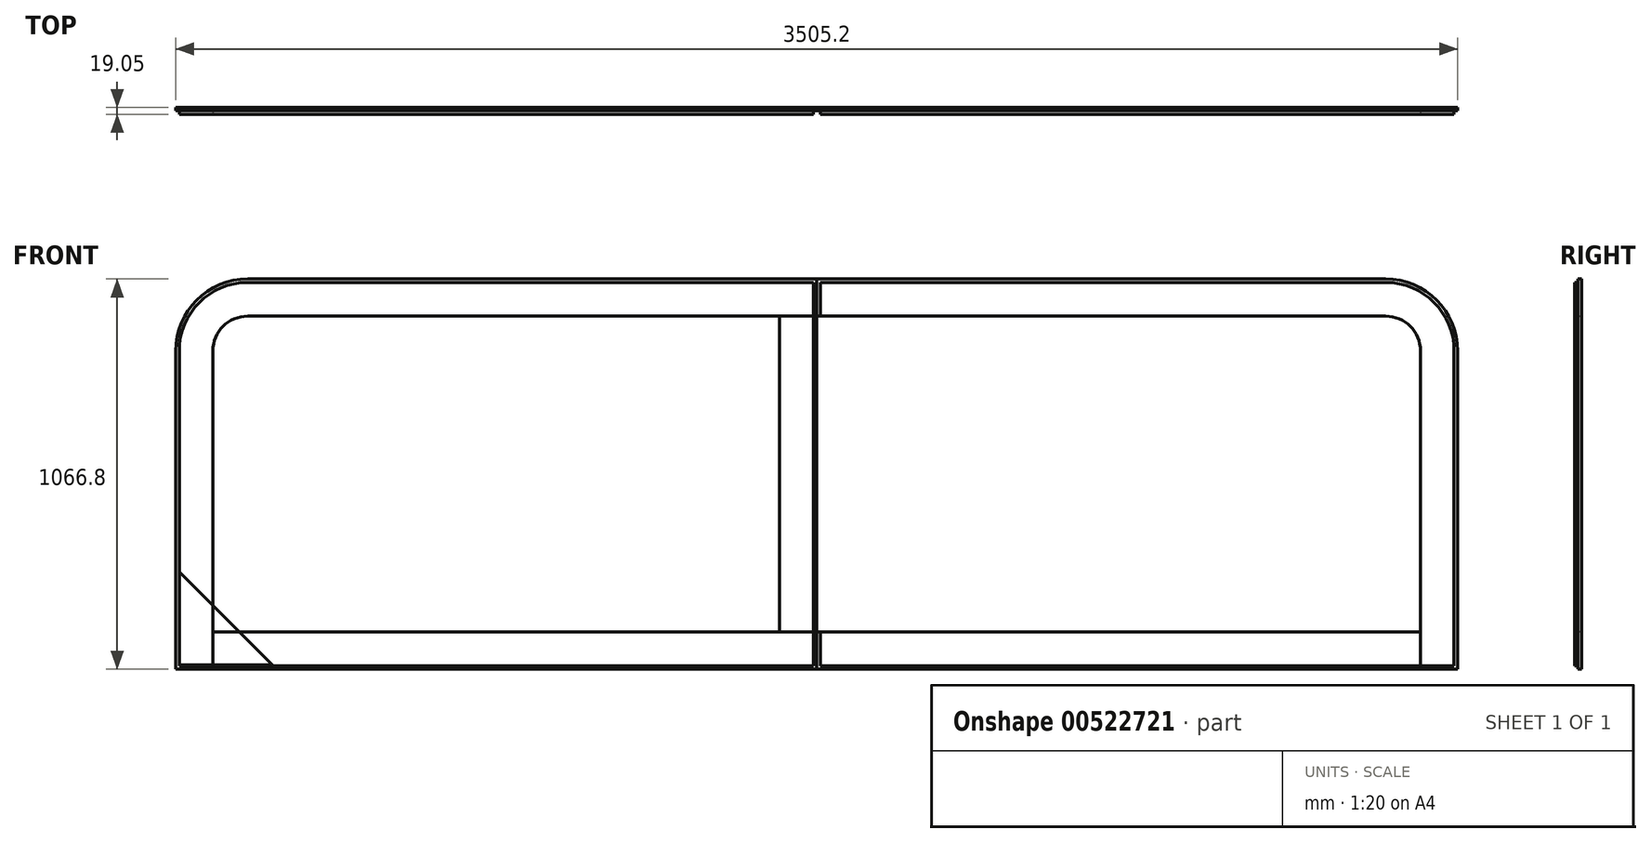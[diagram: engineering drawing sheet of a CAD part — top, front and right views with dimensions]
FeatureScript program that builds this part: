
annotation { "Feature Type Name" : "Feature", "Feature Type Description" : "" }
export const myFeature = defineFeature(function(context is Context, id is Id, definition is map)
    precondition{}
    {
        {
            var Q0;
            Q0=qCreatedBy(makeId("Front.planeOp"),FACE);
            var sketch = newSketch(context, id + "F0", { "sketchPlane" : qUnion([Q0])});
            skLineSegment(sketch, "E0.bottom", {"start": v(1752.6, -533.4) * mm, "end": v(-1752.6, -533.4) * mm});
            skLineSegment(sketch, "E0.top", {"start": v(1555.75, 533.4) * mm, "end": v(-1555.75, 533.4) * mm});
            skLineSegment(sketch, "E0.left", {"start": v(1752.6, -533.4) * mm, "end": v(1752.6, 336.55) * mm});
            skLineSegment(sketch, "E0.right", {"start": v(-1752.6, -533.4) * mm, "end": v(-1752.6, 336.55) * mm});
            skPoint(sketch, "E0.middle", {"position": v(0, 0) * mm});
            skPoint(sketch, "E1.visualSharp", {"position": v(-1752.6, 533.4) * mm});
            skArc(sketch, "E1.filletArc", {"start": v(-1555.75, 533.4) * mm, "mid": v(-1694.94, 475.74) * mm, "end": v(-1752.6, 336.55) * mm});
            skPoint(sketch, "E2.visualSharp", {"position": v(1752.6, 533.4) * mm});
            skArc(sketch, "E2.filletArc", {"start": v(1752.6, 336.55) * mm, "mid": v(1694.94, 475.74) * mm, "end": v(1555.75, 533.4) * mm});
            skArc(sketch, "E3.0", {"start": v(1651, 336.55) * mm, "mid": v(1623.1, 403.9) * mm, "end": v(1555.75, 431.8) * mm});
            skArc(sketch, "E3.1", {"start": v(-1555.75, 431.8) * mm, "mid": v(-1623.1, 403.9) * mm, "end": v(-1651, 336.55) * mm});
            skLineSegment(sketch, "E3.2", {"start": v(-1651, -431.8) * mm, "end": v(-1651, 336.55) * mm});
            skLineSegment(sketch, "E3.3", {"start": v(1555.75, 431.8) * mm, "end": v(-1555.75, 431.8) * mm});
            skLineSegment(sketch, "E3.4", {"start": v(1651, -431.8) * mm, "end": v(-1651, -431.8) * mm});
            skLineSegment(sketch, "E3.5", {"start": v(1651, -431.8) * mm, "end": v(1651, 336.55) * mm});
            skSolve(sketch);
        }
        {
            var Q0;
            Q0 = qSketchRegion(id + "F0", true);
            extrude(context, id + "F1", {"entities" : qUnion([Q0]), "depth" : 19.05 * mm, "offsetDistance" : 25.4 * mm});
        }
        {
            var Q0;
            Q0=makeQuery(id+"F1.opExtrude","CAP_FACE",FACE,{"disambiguationData":[OSD([sQuery(id+"F0.wireOp",EDGE,"E0.bottom"),sQuery(id+"F0.wireOp",EDGE,"E0.top"),sQuery(id+"F0.wireOp",EDGE,"E0.left"),sQuery(id+"F0.wireOp",EDGE,"E0.right"),sQuery(id+"F0.wireOp",EDGE,"E1.filletArc"),sQuery(id+"F0.wireOp",EDGE,"E2.filletArc"),sQuery(id+"F0.wireOp",EDGE,"E3.0"),sQuery(id+"F0.wireOp",EDGE,"E3.1"),sQuery(id+"F0.wireOp",EDGE,"E3.2"),sQuery(id+"F0.wireOp",EDGE,"E3.3"),sQuery(id+"F0.wireOp",EDGE,"E3.4"),sQuery(id+"F0.wireOp",EDGE,"E3.5")])],"isStart":false});
            var sketch = newSketch(context, id + "F2", { "sketchPlane" : qUnion([Q0])});
            skLineSegment(sketch, "E4.bottom", {"start": v(0, 533.4) * mm, "end": v(-2438.4, 533.4) * mm});
            skLineSegment(sketch, "E4.top", {"start": v(0, -711.2) * mm, "end": v(-2438.4, -711.2) * mm});
            skLineSegment(sketch, "E4.left", {"start": v(0, 533.4) * mm, "end": v(0, -711.2) * mm});
            skLineSegment(sketch, "E4.right", {"start": v(-2438.4, 533.4) * mm, "end": v(-2438.4, -711.2) * mm});
            skSolve(sketch);
        }
        {
            var Q0;
            {var subQ6=makeQuery(id+"F1.opExtrude","CAP_EDGE",EDGE,{"disambiguationData":[OSD([sQuery(id+"F0.wireOp",EDGE,"E0.right")])],"isStart":false});Q0=makeQuery(id+"F2.imprint","IMPRINT",FACE,{"disambiguationData":[TD([[makeQuery(id+"F2.imprint","IMPRINT",EDGE,{"derivedFrom":subQ6}),-1.0]])]});}
            var sketch = newSketch(context, id + "F3", { "sketchPlane" : qUnion([Q0])});
            skLineSegment(sketch, "E5.bottom", {"start": v(-1651, -395.78) * mm, "end": v(0, -395.78) * mm});
            skLineSegment(sketch, "E5.top", {"start": v(-1651, -590.4) * mm, "end": v(0, -590.4) * mm});
            skLineSegment(sketch, "E5.left", {"start": v(-1651, -395.78) * mm, "end": v(-1651, -590.4) * mm});
            skLineSegment(sketch, "E5.right", {"start": v(0, -395.78) * mm, "end": v(0, -590.4) * mm});
            skSolve(sketch);
        }
        {
            var Q0;
            Q0 = qSketchRegion(id + "F3", true);
            extrude(context, id + "F4", {"entities" : qUnion([Q0]), "operationType" : NewBodyOperationType.REMOVE, "endBound" : BoundingType.THROUGH_ALL, "oppositeDirection" : true, "depth" : 25.4 * mm, "offsetDistance" : 25.4 * mm});
        }
        {
            var Q0;
            {var subQ6=makeQuery(id+"F1.opExtrude","CAP_EDGE",EDGE,{"disambiguationData":[OSD([sQuery(id+"F0.wireOp",EDGE,"E0.right")])],"isStart":false});Q0=makeQuery(id+"F2.imprint","IMPRINT",FACE,{"disambiguationData":[TD([[makeQuery(id+"F2.imprint","IMPRINT",EDGE,{"derivedFrom":subQ6}),-1.0]])]});}
            var sketch = newSketch(context, id + "F5", { "sketchPlane" : qUnion([Q0])});
            skLineSegment(sketch, "E6.0", {"start": v(-1743.08, -523.88) * mm, "end": v(-1743.08, 336.55) * mm});
            skArc(sketch, "E6.1", {"start": v(-1555.75, 523.88) * mm, "mid": v(-1688.2, 469) * mm, "end": v(-1743.08, 336.55) * mm});
            skLineSegment(sketch, "E6.2", {"start": v(161.15, 523.88) * mm, "end": v(-1555.75, 523.88) * mm});
            skLineSegment(sketch, "E7", {"start": v(-1743.08, -533.4) * mm, "end": v(-1752.6, -533.4) * mm});
            skLineSegment(sketch, "E8", {"start": v(-1752.6, -533.4) * mm, "end": v(-1752.6, 336.55) * mm});
            skLineSegment(sketch, "E9", {"start": v(-1752.6, 336.55) * mm, "end": v(-1752.6, 336.55) * mm});
            skLineSegment(sketch, "E10", {"start": v(161.15, 533.4) * mm, "end": v(-1555.75, 533.4) * mm});
            skLineSegment(sketch, "E11", {"start": v(161.15, 533.4) * mm, "end": v(161.15, 523.88) * mm});
            skArc(sketch, "E12.filletArc", {"start": v(-1555.75, 533.4) * mm, "mid": v(-1694.94, 475.74) * mm, "end": v(-1752.6, 336.55) * mm});
            skLineSegment(sketch, "E13.bottom", {"start": v(-1743.08, -533.4) * mm, "end": v(-1651, -533.4) * mm});
            skLineSegment(sketch, "E13.top", {"start": v(-1743.08, -523.88) * mm, "end": v(-1651, -523.88) * mm});
            skLineSegment(sketch, "E13.right", {"start": v(-1651, -533.4) * mm, "end": v(-1651, -523.88) * mm});
            skSolve(sketch);
        }
        {
            var Q0;
            Q0 = qSketchRegion(id + "F5", true);
            extrude(context, id + "F6", {"entities" : qUnion([Q0]), "operationType" : NewBodyOperationType.REMOVE, "oppositeDirection" : true, "depth" : 9.52 * mm, "offsetDistance" : 25.4 * mm});
        }
        {
            var Q0;
            Q0=makeQuery(id+"F1.opExtrude","CAP_FACE",FACE,{"disambiguationData":[OSD([sQuery(id+"F0.wireOp",EDGE,"E0.bottom"),sQuery(id+"F0.wireOp",EDGE,"E0.top"),sQuery(id+"F0.wireOp",EDGE,"E0.left"),sQuery(id+"F0.wireOp",EDGE,"E0.right"),sQuery(id+"F0.wireOp",EDGE,"E1.filletArc"),sQuery(id+"F0.wireOp",EDGE,"E2.filletArc"),sQuery(id+"F0.wireOp",EDGE,"E3.0"),sQuery(id+"F0.wireOp",EDGE,"E3.1"),sQuery(id+"F0.wireOp",EDGE,"E3.2"),sQuery(id+"F0.wireOp",EDGE,"E3.3"),sQuery(id+"F0.wireOp",EDGE,"E3.4"),sQuery(id+"F0.wireOp",EDGE,"E3.5")])],"isStart":false});
            var sketch = newSketch(context, id + "F7", { "sketchPlane" : qUnion([Q0])});
            skLineSegment(sketch, "E14.bottom", {"start": v(0, 635.38) * mm, "end": v(1845.03, 635.38) * mm});
            skLineSegment(sketch, "E14.top", {"start": v(0, -691.48) * mm, "end": v(1845.03, -691.48) * mm});
            skLineSegment(sketch, "E14.left", {"start": v(0, 635.38) * mm, "end": v(0, -691.48) * mm});
            skLineSegment(sketch, "E14.right", {"start": v(1845.03, 635.38) * mm, "end": v(1845.03, -691.48) * mm});
            skSolve(sketch);
        }
        {
            var Q0;
            Q0 = qSketchRegion(id + "F7", true);
            extrude(context, id + "F8", {"entities" : qUnion([Q0]), "operationType" : NewBodyOperationType.REMOVE, "endBound" : BoundingType.THROUGH_ALL, "oppositeDirection" : true, "depth" : 25.4 * mm, "offsetDistance" : 25.4 * mm});
        }
        {
            var Q0;
            Q0=qCreatedBy(makeId("Front.planeOp"),FACE);
            var sketch = newSketch(context, id + "F9", { "sketchPlane" : qUnion([Q0])});
            skLineSegment(sketch, "E15", {"start": v(0, 777.45) * mm, "end": v(0, -972.38) * mm, "construction": true});
            skSolve(sketch);
        }
        {
            var Q0;
            Q0=makeQuery(id+"F1.opExtrude","CAP_FACE",FACE,{"disambiguationData":[OSD([sQuery(id+"F0.wireOp",EDGE,"E0.bottom"),sQuery(id+"F0.wireOp",EDGE,"E0.top"),sQuery(id+"F0.wireOp",EDGE,"E0.left"),sQuery(id+"F0.wireOp",EDGE,"E0.right"),sQuery(id+"F0.wireOp",EDGE,"E1.filletArc"),sQuery(id+"F0.wireOp",EDGE,"E2.filletArc"),sQuery(id+"F0.wireOp",EDGE,"E3.0"),sQuery(id+"F0.wireOp",EDGE,"E3.1"),sQuery(id+"F0.wireOp",EDGE,"E3.2"),sQuery(id+"F0.wireOp",EDGE,"E3.3"),sQuery(id+"F0.wireOp",EDGE,"E3.4"),sQuery(id+"F0.wireOp",EDGE,"E3.5")])],"isStart":false});
            var sketch = newSketch(context, id + "F10", { "sketchPlane" : qUnion([Q0])});
            skLineSegment(sketch, "E16.bottom", {"start": v(-1651, -431.8) * mm, "end": v(0, -431.8) * mm});
            skLineSegment(sketch, "E16.top", {"start": v(-1651, -533.4) * mm, "end": v(0, -533.4) * mm});
            skLineSegment(sketch, "E16.left", {"start": v(-1651, -431.8) * mm, "end": v(-1651, -533.4) * mm});
            skLineSegment(sketch, "E16.right", {"start": v(0, -431.8) * mm, "end": v(0, -533.4) * mm});
            skSolve(sketch);
        }
        {
            var Q0;
            Q0 = qSketchRegion(id + "F10", true);
            extrude(context, id + "F11", {"entities" : qUnion([Q0]), "oppositeDirection" : true, "depth" : 19.05 * mm, "offsetDistance" : 25.4 * mm});
        }
        {
            var Q0;
            Q0=makeQuery(id+"F11.opExtrude","CAP_FACE",FACE,{"disambiguationData":[OSD([sQuery(id+"F10.wireOp",EDGE,"E16.bottom"),sQuery(id+"F10.wireOp",EDGE,"E16.top"),sQuery(id+"F10.wireOp",EDGE,"E16.left"),sQuery(id+"F10.wireOp",EDGE,"E16.right")])],"isStart":true});
            var sketch = newSketch(context, id + "F12", { "sketchPlane" : qUnion([Q0])});
            skLineSegment(sketch, "E17.bottom", {"start": v(-1651, -523.88) * mm, "end": v(0, -523.88) * mm});
            skLineSegment(sketch, "E17.top", {"start": v(-1651, -533.4) * mm, "end": v(0, -533.4) * mm});
            skLineSegment(sketch, "E17.left", {"start": v(-1651, -523.88) * mm, "end": v(-1651, -533.4) * mm});
            skLineSegment(sketch, "E17.right", {"start": v(0, -523.88) * mm, "end": v(0, -533.4) * mm});
            skSolve(sketch);
        }
        {
            var Q0;
            Q0 = qSketchRegion(id + "F12", true);
            extrude(context, id + "F13", {"entities" : qUnion([Q0]), "operationType" : NewBodyOperationType.REMOVE, "oppositeDirection" : true, "depth" : 9.52 * mm, "offsetDistance" : 25.4 * mm});
        }
        {
            var Q0;
            Q0=makeQuery(id+"F1.opExtrude","CAP_FACE",FACE,{"disambiguationData":[OSD([sQuery(id+"F0.wireOp",EDGE,"E0.bottom"),sQuery(id+"F0.wireOp",EDGE,"E0.top"),sQuery(id+"F0.wireOp",EDGE,"E0.left"),sQuery(id+"F0.wireOp",EDGE,"E0.right"),sQuery(id+"F0.wireOp",EDGE,"E1.filletArc"),sQuery(id+"F0.wireOp",EDGE,"E2.filletArc"),sQuery(id+"F0.wireOp",EDGE,"E3.0"),sQuery(id+"F0.wireOp",EDGE,"E3.1"),sQuery(id+"F0.wireOp",EDGE,"E3.2"),sQuery(id+"F0.wireOp",EDGE,"E3.3"),sQuery(id+"F0.wireOp",EDGE,"E3.4"),sQuery(id+"F0.wireOp",EDGE,"E3.5")])],"isStart":false});
            var sketch = newSketch(context, id + "F14", { "sketchPlane" : qUnion([Q0])});
            skLineSegment(sketch, "E18.bottom", {"start": v(0, 523.88) * mm, "end": v(-9.52, 523.88) * mm});
            skLineSegment(sketch, "E18.top", {"start": v(0, 431.8) * mm, "end": v(-9.52, 431.8) * mm});
            skLineSegment(sketch, "E18.left", {"start": v(0, 523.88) * mm, "end": v(0, 431.8) * mm});
            skLineSegment(sketch, "E18.right", {"start": v(-9.52, 523.88) * mm, "end": v(-9.52, 431.8) * mm});
            skSolve(sketch);
        }
        {
            var Q0;
            Q0 = qSketchRegion(id + "F14", true);
            extrude(context, id + "F15", {"entities" : qUnion([Q0]), "operationType" : NewBodyOperationType.REMOVE, "oppositeDirection" : true, "depth" : 9.52 * mm, "offsetDistance" : 25.4 * mm});
        }
        {
            var Q0;
            Q0=makeQuery(id+"F11.opExtrude","CAP_FACE",FACE,{"disambiguationData":[OSD([sQuery(id+"F10.wireOp",EDGE,"E16.bottom"),sQuery(id+"F10.wireOp",EDGE,"E16.top"),sQuery(id+"F10.wireOp",EDGE,"E16.left"),sQuery(id+"F10.wireOp",EDGE,"E16.right")])],"isStart":true});
            var sketch = newSketch(context, id + "F16", { "sketchPlane" : qUnion([Q0])});
            skLineSegment(sketch, "E19.bottom", {"start": v(0, -431.8) * mm, "end": v(-9.53, -431.8) * mm});
            skLineSegment(sketch, "E19.top", {"start": v(0, -523.88) * mm, "end": v(-9.52, -523.88) * mm});
            skLineSegment(sketch, "E19.left", {"start": v(0, -431.8) * mm, "end": v(0, -523.88) * mm});
            skLineSegment(sketch, "E19.right", {"start": v(-9.53, -431.8) * mm, "end": v(-9.52, -523.88) * mm});
            skSolve(sketch);
        }
        {
            var Q0;
            Q0 = qSketchRegion(id + "F16", true);
            extrude(context, id + "F17", {"entities" : qUnion([Q0]), "operationType" : NewBodyOperationType.REMOVE, "oppositeDirection" : true, "depth" : 9.52 * mm, "offsetDistance" : 25.4 * mm});
        }
        {
            var Q0;
            Q0=qCreatedBy(makeId("Front.planeOp"),FACE);
            var sketch = newSketch(context, id + "F18", { "sketchPlane" : qUnion([Q0])});
            skLineSegment(sketch, "E20.bottom", {"start": v(0, 431.8) * mm, "end": v(-101.6, 431.8) * mm});
            skLineSegment(sketch, "E20.top", {"start": v(0, -431.8) * mm, "end": v(-101.6, -431.8) * mm});
            skLineSegment(sketch, "E20.left", {"start": v(0, 431.8) * mm, "end": v(0, -431.8) * mm});
            skLineSegment(sketch, "E20.right", {"start": v(-101.6, 431.8) * mm, "end": v(-101.6, -431.8) * mm});
            skSolve(sketch);
        }
        {
            var Q0;
            Q0 = qSketchRegion(id + "F18", true);
            extrude(context, id + "F19", {"entities" : qUnion([Q0]), "depth" : 19.05 * mm, "offsetDistance" : 25.4 * mm});
        }
        {
            var Q0;
            Q0=makeQuery(id+"F19.opExtrude","CAP_FACE",FACE,{"disambiguationData":[OSD([sQuery(id+"F18.wireOp",EDGE,"E20.bottom"),sQuery(id+"F18.wireOp",EDGE,"E20.top"),sQuery(id+"F18.wireOp",EDGE,"E20.left"),sQuery(id+"F18.wireOp",EDGE,"E20.right")])],"isStart":false});
            var sketch = newSketch(context, id + "F20", { "sketchPlane" : qUnion([Q0])});
            skLineSegment(sketch, "E21.bottom", {"start": v(0, 431.8) * mm, "end": v(-9.53, 431.8) * mm});
            skLineSegment(sketch, "E21.top", {"start": v(0, -431.8) * mm, "end": v(-9.52, -431.8) * mm});
            skLineSegment(sketch, "E21.left", {"start": v(0, 431.8) * mm, "end": v(0, -431.8) * mm});
            skLineSegment(sketch, "E21.right", {"start": v(-9.53, 431.8) * mm, "end": v(-9.52, -431.8) * mm});
            skSolve(sketch);
        }
        {
            var Q0;
            Q0 = qSketchRegion(id + "F20", true);
            extrude(context, id + "F21", {"entities" : qUnion([Q0]), "operationType" : NewBodyOperationType.REMOVE, "oppositeDirection" : true, "depth" : 9.52 * mm, "offsetDistance" : 25.4 * mm});
        }
        {
            var Q0;
            Q0=makeQuery(id+"F1.opExtrude","SWEPT_BODY",BODY,{"disambiguationData":[OSD([sQuery(id+"F0.wireOp",EDGE,"E0.bottom"),sQuery(id+"F0.wireOp",EDGE,"E0.top"),sQuery(id+"F0.wireOp",EDGE,"E0.left"),sQuery(id+"F0.wireOp",EDGE,"E0.right"),sQuery(id+"F0.wireOp",EDGE,"E1.filletArc"),sQuery(id+"F0.wireOp",EDGE,"E2.filletArc"),sQuery(id+"F0.wireOp",EDGE,"E3.0"),sQuery(id+"F0.wireOp",EDGE,"E3.1"),sQuery(id+"F0.wireOp",EDGE,"E3.2"),sQuery(id+"F0.wireOp",EDGE,"E3.3"),sQuery(id+"F0.wireOp",EDGE,"E3.4"),sQuery(id+"F0.wireOp",EDGE,"E3.5")])]});
            var Q1;
            Q1=qCreatedBy(makeId("Right.planeOp"),FACE);
            mirror(context, id + "F22", {"entities" : qUnion([Q0]), "mirrorPlane" : qUnion([Q1])});
        }
        {
            var Q0;
            Q0=qCreatedBy(makeId("Front.planeOp"),FACE);
            var sketch = newSketch(context, id + "F23", { "sketchPlane" : qUnion([Q0])});
            skLineSegment(sketch, "E22", {"start": v(-1743.08, -267.66) * mm, "end": v(-1743.08, -521.66) * mm});
            skLineSegment(sketch, "E23", {"start": v(-1743.08, -521.66) * mm, "end": v(-1489.07, -521.66) * mm});
            skLineSegment(sketch, "E24", {"start": v(-1489.07, -521.66) * mm, "end": v(-1743.08, -267.66) * mm});
            skSolve(sketch);
        }
        {
            var Q0;
            Q0 = qSketchRegion(id + "F23", true);
            extrude(context, id + "F24", {"entities" : qUnion([Q0]), "depth" : 19.05 * mm, "offsetDistance" : 25.4 * mm});
        }
        {
            var Q0;
            Q0=makeQuery(id+"F11.opExtrude","SWEPT_BODY",BODY,{"disambiguationData":[OSD([sQuery(id+"F10.wireOp",EDGE,"E16.bottom"),sQuery(id+"F10.wireOp",EDGE,"E16.top"),sQuery(id+"F10.wireOp",EDGE,"E16.left"),sQuery(id+"F10.wireOp",EDGE,"E16.right")])]});
            var Q1;
            Q1=qCreatedBy(makeId("Right.planeOp"),FACE);
            mirror(context, id + "F25", {"entities" : qUnion([Q0]), "mirrorPlane" : qUnion([Q1])});
        }
    });
